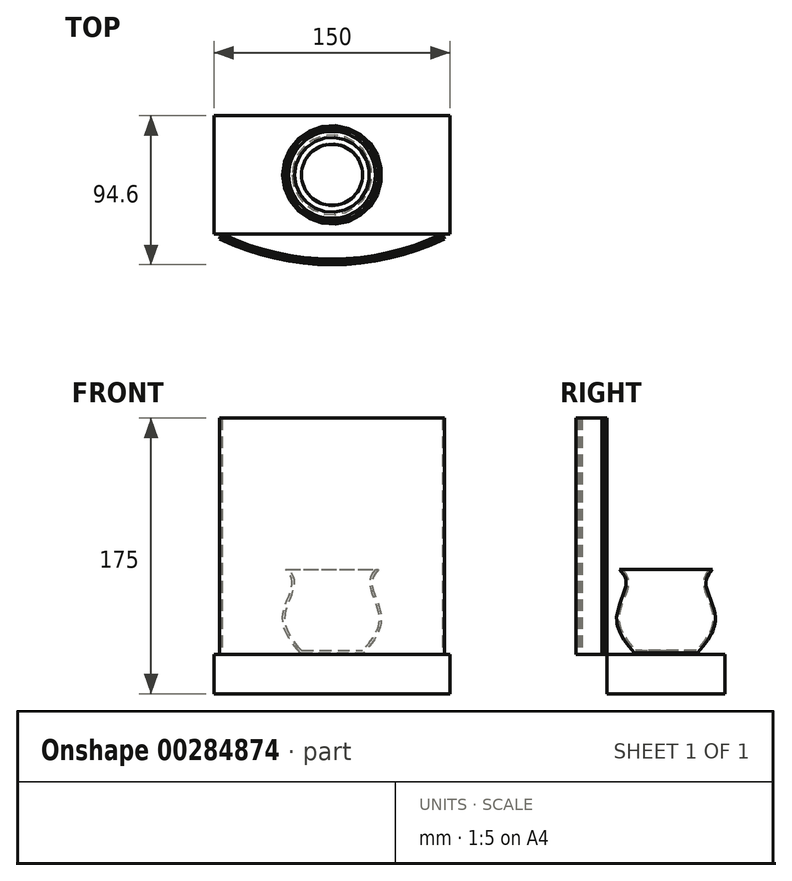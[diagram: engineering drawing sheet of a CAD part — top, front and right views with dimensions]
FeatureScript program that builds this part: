
annotation { "Feature Type Name" : "Feature", "Feature Type Description" : "" }
export const myFeature = defineFeature(function(context is Context, id is Id, definition is map)
    precondition{}
    {
        {
            var Q0;
            Q0=qCreatedBy(makeId("Top.planeOp"),FACE);
            var sketch = newSketch(context, id + "F0", { "sketchPlane" : qUnion([Q0])});
            skLineSegment(sketch, "E0.bottom", {"start": v(75, 37.5) * mm, "end": v(-75, 37.5) * mm});
            skLineSegment(sketch, "E0.top", {"start": v(75, -37.5) * mm, "end": v(-75, -37.5) * mm});
            skLineSegment(sketch, "E0.left", {"start": v(75, 37.5) * mm, "end": v(75, -37.5) * mm});
            skLineSegment(sketch, "E0.right", {"start": v(-75, 37.5) * mm, "end": v(-75, -37.5) * mm});
            skPoint(sketch, "E0.middle", {"position": v(0, 0) * mm});
            skSolve(sketch);
        }
        {
            var Q0;
            Q0 = qSketchRegion(id + "F0", true);
            extrude(context, id + "F1", {"entities" : qUnion([Q0]), "depth" : 25 * mm});
        }
        {
            var Q0;
            Q0=makeQuery(id+"F1.opExtrude","CAP_FACE",FACE,{"disambiguationData":[OSD([sQuery(id+"F0.wireOp",EDGE,"E0.bottom"),sQuery(id+"F0.wireOp",EDGE,"E0.top"),sQuery(id+"F0.wireOp",EDGE,"E0.left"),sQuery(id+"F0.wireOp",EDGE,"E0.right")])],"isStart":false});
            var sketch = newSketch(context, id + "F2", { "sketchPlane" : qUnion([Q0])});
            skArc(sketch, "E1", {"start": v(-70, -37.5) * mm, "mid": v(0, -53.5) * mm, "end": v(70, -37.5) * mm});
            skArc(sketch, "E2.0", {"start": v(-70.52, -38.58) * mm, "mid": v(0, -54.7) * mm, "end": v(70.52, -38.58) * mm});
            skLineSegment(sketch, "E3", {"start": v(70, -37.5) * mm, "end": v(70.52, -38.58) * mm});
            skLineSegment(sketch, "E4", {"start": v(-70.52, -38.58) * mm, "end": v(-70, -37.5) * mm});
            skSolve(sketch);
        }
        {
            var Q0;
            Q0 = qSketchRegion(id + "F2", true);
            extrude(context, id + "F3", {"entities" : qUnion([Q0]), "depth" : 150 * mm});
        }
        {
            var Q0;
            Q0=makeQuery(id+"F1.opExtrude","CAP_FACE",FACE,{"disambiguationData":[OSD([sQuery(id+"F0.wireOp",EDGE,"E0.bottom"),sQuery(id+"F0.wireOp",EDGE,"E0.top"),sQuery(id+"F0.wireOp",EDGE,"E0.left"),sQuery(id+"F0.wireOp",EDGE,"E0.right")])],"isStart":false});
            var sketch = newSketch(context, id + "F4", { "sketchPlane" : qUnion([Q0])});
            skArc(sketch, "E5.0", {"start": v(-70.52, -38.58) * mm, "mid": v(0, -54.7) * mm, "end": v(70.52, -38.58) * mm});
            skArc(sketch, "E6.0", {"start": v(-71.04, -39.66) * mm, "mid": v(0, -55.9) * mm, "end": v(71.04, -39.66) * mm});
            skLineSegment(sketch, "E7", {"start": v(-70.52, -38.58) * mm, "end": v(-71.04, -39.66) * mm});
            skLineSegment(sketch, "E8", {"start": v(70.52, -38.58) * mm, "end": v(71.04, -39.66) * mm});
            skSolve(sketch);
        }
        {
            var Q0;
            Q0 = qSketchRegion(id + "F4", true);
            extrude(context, id + "F5", {"entities" : qUnion([Q0]), "depth" : 150 * mm});
        }
        {
            var Q0;
            Q0=makeQuery(id+"F1.opExtrude","CAP_FACE",FACE,{"disambiguationData":[OSD([sQuery(id+"F0.wireOp",EDGE,"E0.bottom"),sQuery(id+"F0.wireOp",EDGE,"E0.top"),sQuery(id+"F0.wireOp",EDGE,"E0.left"),sQuery(id+"F0.wireOp",EDGE,"E0.right")])],"isStart":false});
            var sketch = newSketch(context, id + "F6", { "sketchPlane" : qUnion([Q0])});
            skArc(sketch, "E9.0", {"start": v(-71.04, -39.66) * mm, "mid": v(0, -55.9) * mm, "end": v(71.04, -39.66) * mm});
            skArc(sketch, "E10.0", {"start": v(-71.56, -40.74) * mm, "mid": v(0, -57.1) * mm, "end": v(71.56, -40.74) * mm});
            skLineSegment(sketch, "E11", {"start": v(-71.04, -39.66) * mm, "end": v(-71.56, -40.74) * mm});
            skLineSegment(sketch, "E12", {"start": v(71.04, -39.66) * mm, "end": v(71.56, -40.74) * mm});
            skSolve(sketch);
        }
        {
            var Q0;
            Q0=makeQuery(id+"F6.imprint","IMPRINT",FACE,{"disambiguationData":[TD([[makeQuery(id+"F6.imprint","IMPRINT",EDGE,{"derivedFrom":sQuery(id+"F6.wireOp",EDGE,"E9.0")}),-1.0]])]});
            extrude(context, id + "F7", {"entities" : qUnion([Q0]), "depth" : 150 * mm});
        }
        {
            var Q0;
            Q0=qCreatedBy(makeId("Front.planeOp"),FACE);
            var sketch = newSketch(context, id + "F8", { "sketchPlane" : qUnion([Q0])});
            skLineSegment(sketch, "E13", {"start": v(0, 38.8) * mm, "end": v(0, 134.49) * mm, "construction": true});
            skPoint(sketch, "E14.start.orphan", {"position": v(0, 26) * mm});
            skLineSegment(sketch, "E15", {"start": v(0, 26) * mm, "end": v(20, 26) * mm});
            skFitSpline(sketch, "E16", {"points": [v(20, 26) * mm, v(31.33, 48) * mm, v(25.3, 70.44) * mm, v(29.65, 78.82) * mm], "startDerivative": vector(45.2, 48.66) * mm, "endDerivative": vector(27.51, 29.03) * mm});
            skLineSegment(sketch, "E17", {"start": v(29.65, 78.82) * mm, "end": v(0, 78.82) * mm});
            skLineSegment(sketch, "E18", {"start": v(0, 78.82) * mm, "end": v(0, 26) * mm});
            skSolve(sketch);
        }
        {
            var Q0;
            Q0 = qSketchRegion(id + "F8", true);
            var Q1;
            Q1=sQuery(id+"F8.wireOp",EDGE,"E13");
            revolve(context, id + "F9", {"entities" : qUnion([Q0]), "axis" : qUnion([Q1]), "revolveType" : RevolveType.FULL});
        }
        {
            var Q0;
            Q0=makeQuery(id+"F9.opRevolve","SWEPT_FACE",FACE,{"disambiguationData":[OSD([sQuery(id+"F8.wireOp",EDGE,"E17")])]});
            shell(context, id + "F10", {"entities" : qUnion([Q0]), "thickness" : 1.5 * mm});
        }
    });
